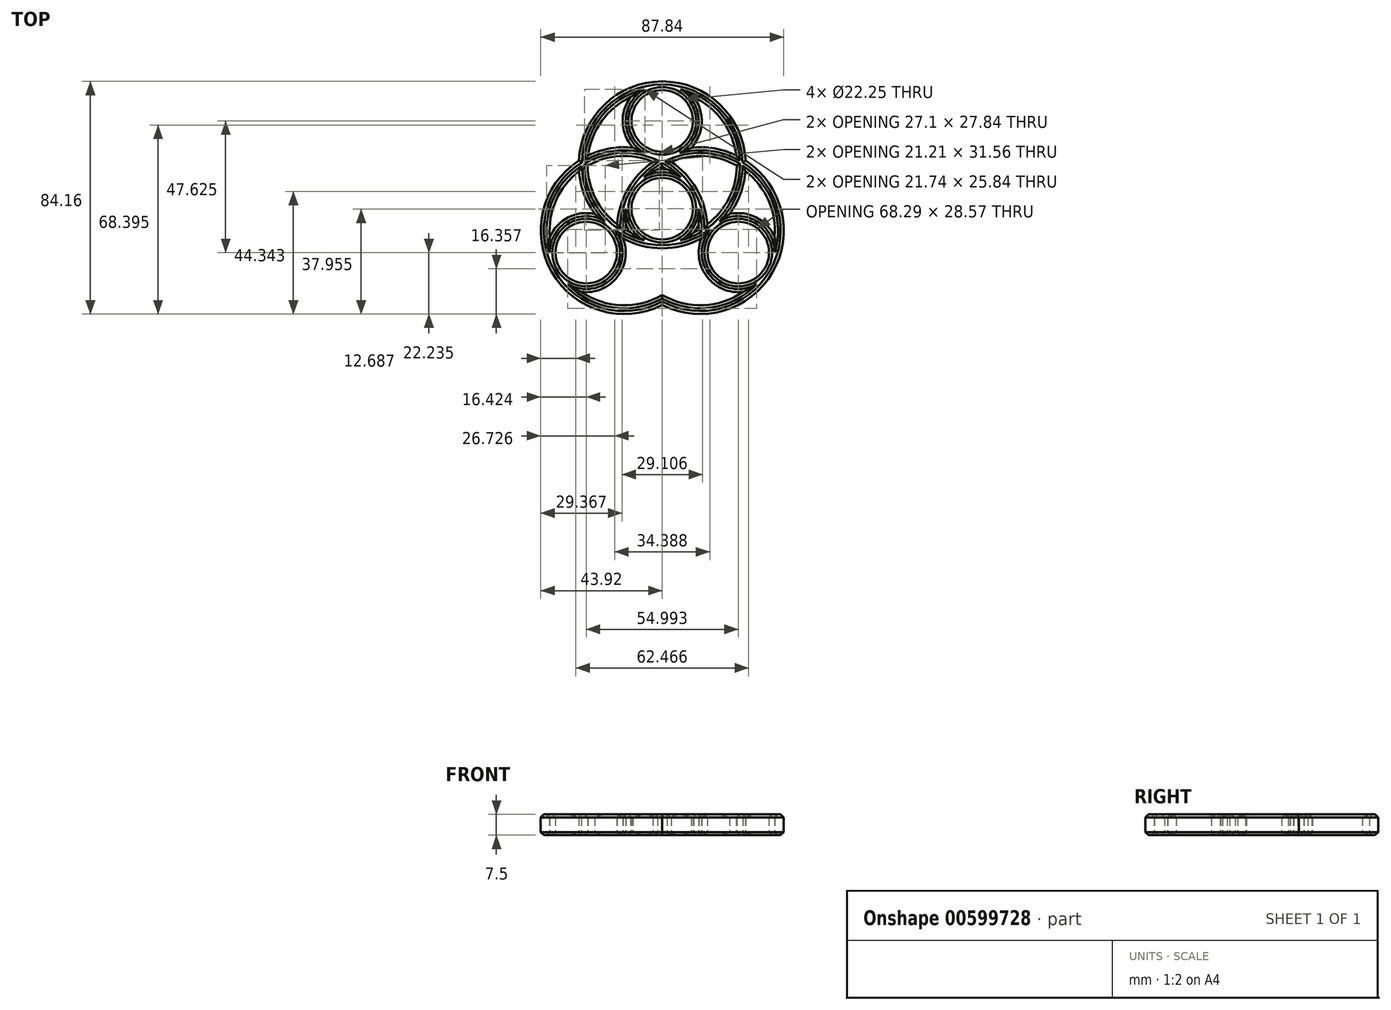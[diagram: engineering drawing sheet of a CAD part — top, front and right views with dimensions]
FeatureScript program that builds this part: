
annotation { "Feature Type Name" : "Feature", "Feature Type Description" : "" }
export const myFeature = defineFeature(function(context is Context, id is Id, definition is map)
    precondition{}
    {
        {
            var Q0;
            Q0=qCreatedBy(makeId("Top.planeOp"),FACE);
            var sketch = newSketch(context, id + "F0", { "sketchPlane" : qUnion([Q0])});
            skCircle(sketch, "E0", {"center": v(0, 0) * mm, "radius": 11.12 * mm});
            skCircle(sketch, "E1", {"center": v(0, 31.75) * mm, "radius": 11.12 * mm});
            skCircle(sketch, "E2", {"center": v(0, 31.75) * mm, "radius": 14.3 * mm});
            skCircle(sketch, "E3", {"center": v(0, 0) * mm, "radius": 14.3 * mm});
            skCircle(sketch, "E4", {"center": v(0, 15.88) * mm, "radius": 30.18 * mm});
            skCircle(sketch, "E5", {"center": v(0, 15.88) * mm, "radius": 27 * mm});
            skCircle(sketch, "E6.1.0", {"center": v(-27.5, -15.87) * mm, "radius": 11.12 * mm});
            skCircle(sketch, "E6.1.1", {"center": v(-27.5, -15.87) * mm, "radius": 14.3 * mm});
            skCircle(sketch, "E6.1.2", {"center": v(-13.75, -7.94) * mm, "radius": 27 * mm});
            skCircle(sketch, "E6.1.3", {"center": v(-13.75, -7.94) * mm, "radius": 30.18 * mm});
            skCircle(sketch, "E6.2.0", {"center": v(27.5, -15.88) * mm, "radius": 11.12 * mm});
            skCircle(sketch, "E6.2.1", {"center": v(27.5, -15.88) * mm, "radius": 14.3 * mm});
            skCircle(sketch, "E6.2.2", {"center": v(13.75, -7.94) * mm, "radius": 27 * mm});
            skCircle(sketch, "E6.2.3", {"center": v(13.75, -7.94) * mm, "radius": 30.18 * mm});
            skSolve(sketch);
        }
        {
            var Q0;
            Q0 = qSketchRegion(id + "F0", true);
            var Q1;
            {var subQ0=sQuery(id+"F0.wireOp",EDGE,"E6.1.3");var subQ1=sQuery(id+"F0.wireOp",EDGE,"E1");var subQ2=makeQuery(id+"F0.imprint","INTERSECT",VERTEX,{"disambiguationData":[OD(0.0)],"derivedFrom":[subQ1,subQ0]});Q1=makeQuery(id+"F0.imprint","IMPRINT",FACE,{"disambiguationData":[TD([[makeQuery(id+"F0.imprint","IMPRINT",EDGE,{"disambiguationData":[TD([[subQ2,1.0]])],"derivedFrom":subQ1}),-1.0]])]});}
            var Q2;
            {var subQ0=sQuery(id+"F0.wireOp",EDGE,"E5");var subQ1=sQuery(id+"F0.wireOp",EDGE,"E1");var subQ2=makeQuery(id+"F0.imprint","INTERSECT",VERTEX,{"derivedFrom":[subQ1,subQ0]});Q2=makeQuery(id+"F0.imprint","IMPRINT",FACE,{"disambiguationData":[TD([[makeQuery(id+"F0.imprint","IMPRINT",EDGE,{"disambiguationData":[TD([[subQ2,1.0]])],"derivedFrom":subQ1}),-1.0]])]});}
            var Q3;
            {var subQ0=sQuery(id+"F0.wireOp",EDGE,"E6.1.1");var subQ1=sQuery(id+"F0.wireOp",EDGE,"E4");var subQ2=makeQuery(id+"F0.imprint","INTERSECT",VERTEX,{"disambiguationData":[OD(0.0)],"derivedFrom":[subQ1,subQ0]});Q3=makeQuery(id+"F0.imprint","IMPRINT",FACE,{"disambiguationData":[TD([[makeQuery(id+"F0.imprint","IMPRINT",EDGE,{"disambiguationData":[TD([[subQ2,-1.0]])],"derivedFrom":subQ1}),-1.0]])]});}
            var Q4;
            {var subQ0=sQuery(id+"F0.wireOp",EDGE,"E6.2.3");var subQ1=sQuery(id+"F0.wireOp",EDGE,"E6.1.0");var subQ2=makeQuery(id+"F0.imprint","INTERSECT",VERTEX,{"disambiguationData":[OD(0.0)],"derivedFrom":[subQ1,subQ0]});Q4=makeQuery(id+"F0.imprint","IMPRINT",FACE,{"disambiguationData":[TD([[makeQuery(id+"F0.imprint","IMPRINT",EDGE,{"disambiguationData":[TD([[subQ2,1.0]])],"derivedFrom":subQ1}),-1.0]])]});}
            var Q5;
            {var subQ0=sQuery(id+"F0.wireOp",EDGE,"E6.2.1");var subQ1=sQuery(id+"F0.wireOp",EDGE,"E6.1.3");var subQ2=makeQuery(id+"F0.imprint","INTERSECT",VERTEX,{"disambiguationData":[OD(0.0)],"derivedFrom":[subQ1,subQ0]});Q5=makeQuery(id+"F0.imprint","IMPRINT",FACE,{"disambiguationData":[TD([[makeQuery(id+"F0.imprint","IMPRINT",EDGE,{"disambiguationData":[TD([[subQ2,-1.0]])],"derivedFrom":subQ1}),-1.0]])]});}
            var Q6;
            {var subQ0=sQuery(id+"F0.wireOp",EDGE,"E6.2.0");var subQ1=sQuery(id+"F0.wireOp",EDGE,"E4");var subQ2=makeQuery(id+"F0.imprint","INTERSECT",VERTEX,{"disambiguationData":[OD(1.0)],"derivedFrom":[subQ1,subQ0]});Q6=makeQuery(id+"F0.imprint","IMPRINT",FACE,{"disambiguationData":[TD([[makeQuery(id+"F0.imprint","IMPRINT",EDGE,{"disambiguationData":[TD([[subQ2,-1.0]])],"derivedFrom":subQ1}),-1.0]])]});}
            var Q7;
            {var subQ0=sQuery(id+"F0.wireOp",EDGE,"E6.2.2");var subQ1=sQuery(id+"F0.wireOp",EDGE,"E2");var subQ2=makeQuery(id+"F0.imprint","INTERSECT",VERTEX,{"disambiguationData":[OD(1.0)],"derivedFrom":[subQ1,subQ0]});Q7=makeQuery(id+"F0.imprint","IMPRINT",FACE,{"disambiguationData":[TD([[makeQuery(id+"F0.imprint","IMPRINT",EDGE,{"disambiguationData":[TD([[subQ2,-1.0]])],"derivedFrom":subQ1}),-1.0]])]});}
            var Q8;
            {var subQ3=sQuery(id+"F0.wireOp",EDGE,"E6.2.3");var subQ5=sQuery(id+"F0.wireOp",EDGE,"E1");var subQ6=makeQuery(id+"F0.imprint","INTERSECT",VERTEX,{"disambiguationData":[OD(0.0)],"derivedFrom":[subQ5,subQ3]});Q8=makeQuery(id+"F0.imprint","IMPRINT",FACE,{"disambiguationData":[TD([[makeQuery(id+"F0.imprint","IMPRINT",EDGE,{"disambiguationData":[TD([[subQ6,-1.0]])],"derivedFrom":subQ5}),-1.0]])]});}
            var Q9;
            {var subQ6=sQuery(id+"F0.wireOp",EDGE,"E6.1.3");var subQ8=sQuery(id+"F0.wireOp",EDGE,"E1");var subQ9=makeQuery(id+"F0.imprint","INTERSECT",VERTEX,{"disambiguationData":[OD(0.0)],"derivedFrom":[subQ8,subQ6]});Q9=makeQuery(id+"F0.imprint","IMPRINT",FACE,{"disambiguationData":[TD([[makeQuery(id+"F0.imprint","IMPRINT",EDGE,{"disambiguationData":[TD([[subQ9,-1.0]])],"derivedFrom":subQ8}),-1.0]])]});}
            var Q10;
            {var subQ0=sQuery(id+"F0.wireOp",EDGE,"E6.1.3");var subQ1=sQuery(id+"F0.wireOp",EDGE,"E2");var subQ2=makeQuery(id+"F0.imprint","INTERSECT",VERTEX,{"disambiguationData":[OD(0.0)],"derivedFrom":[subQ1,subQ0]});Q10=makeQuery(id+"F0.imprint","IMPRINT",FACE,{"disambiguationData":[TD([[makeQuery(id+"F0.imprint","IMPRINT",EDGE,{"disambiguationData":[TD([[subQ2,-1.0]])],"derivedFrom":subQ1}),-1.0]])]});}
            var Q11;
            {var subQ0=sQuery(id+"F0.wireOp",EDGE,"E6.1.3");var subQ1=sQuery(id+"F0.wireOp",EDGE,"E1");var subQ2=makeQuery(id+"F0.imprint","INTERSECT",VERTEX,{"disambiguationData":[OD(1.0)],"derivedFrom":[subQ1,subQ0]});Q11=makeQuery(id+"F0.imprint","IMPRINT",FACE,{"disambiguationData":[TD([[makeQuery(id+"F0.imprint","IMPRINT",EDGE,{"disambiguationData":[TD([[subQ2,-1.0]])],"derivedFrom":subQ1}),-1.0]])]});}
            var Q12;
            {var subQ0=sQuery(id+"F0.wireOp",EDGE,"E6.2.3");var subQ1=sQuery(id+"F0.wireOp",EDGE,"E2");var subQ2=makeQuery(id+"F0.imprint","INTERSECT",VERTEX,{"disambiguationData":[OD(0.0)],"derivedFrom":[subQ1,subQ0]});Q12=makeQuery(id+"F0.imprint","IMPRINT",FACE,{"disambiguationData":[TD([[makeQuery(id+"F0.imprint","IMPRINT",EDGE,{"disambiguationData":[TD([[subQ2,-1.0]])],"derivedFrom":subQ1}),1.0]])]});}
            var Q13;
            {var subQ1=sQuery(id+"F0.wireOp",EDGE,"E4");var subQ6=sQuery(id+"F0.wireOp",EDGE,"E6.1.1");var subQ7=makeQuery(id+"F0.imprint","INTERSECT",VERTEX,{"disambiguationData":[OD(0.0)],"derivedFrom":[subQ1,subQ6]});Q13=makeQuery(id+"F0.imprint","IMPRINT",FACE,{"disambiguationData":[TD([[makeQuery(id+"F0.imprint","IMPRINT",EDGE,{"disambiguationData":[TD([[subQ7,-1.0]])],"derivedFrom":subQ1}),1.0]])]});}
            var Q14;
            {var subQ1=sQuery(id+"F0.wireOp",EDGE,"E4");var subQ5=sQuery(id+"F0.wireOp",EDGE,"E6.2.3");var subQ11=makeQuery(id+"F0.imprint","INTERSECT",VERTEX,{"disambiguationData":[OD(1.0)],"derivedFrom":[subQ1,subQ5]});Q14=makeQuery(id+"F0.imprint","IMPRINT",FACE,{"disambiguationData":[TD([[makeQuery(id+"F0.imprint","IMPRINT",EDGE,{"disambiguationData":[TD([[subQ11,-1.0]])],"derivedFrom":subQ1}),-1.0]])]});}
            var Q15;
            {var subQ0=sQuery(id+"F0.wireOp",EDGE,"E6.1.0");var subQ1=sQuery(id+"F0.wireOp",EDGE,"E4");var subQ2=makeQuery(id+"F0.imprint","INTERSECT",VERTEX,{"disambiguationData":[OD(1.0)],"derivedFrom":[subQ1,subQ0]});Q15=makeQuery(id+"F0.imprint","IMPRINT",FACE,{"disambiguationData":[TD([[makeQuery(id+"F0.imprint","IMPRINT",EDGE,{"disambiguationData":[TD([[subQ2,-1.0]])],"derivedFrom":subQ1}),-1.0]])]});}
            var Q16;
            {var subQ0=sQuery(id+"F0.wireOp",EDGE,"E6.2.3");var subQ1=sQuery(id+"F0.wireOp",EDGE,"E4");var subQ2=makeQuery(id+"F0.imprint","INTERSECT",VERTEX,{"disambiguationData":[OD(1.0)],"derivedFrom":[subQ1,subQ0]});Q16=makeQuery(id+"F0.imprint","IMPRINT",FACE,{"disambiguationData":[TD([[makeQuery(id+"F0.imprint","IMPRINT",EDGE,{"disambiguationData":[TD([[subQ2,-1.0]])],"derivedFrom":subQ1}),1.0]])]});}
            var Q17;
            {var subQ0=sQuery(id+"F0.wireOp",EDGE,"E6.1.2");var subQ1=sQuery(id+"F0.wireOp",EDGE,"E4");var subQ2=makeQuery(id+"F0.imprint","INTERSECT",VERTEX,{"disambiguationData":[OD(0.0)],"derivedFrom":[subQ1,subQ0]});Q17=makeQuery(id+"F0.imprint","IMPRINT",FACE,{"disambiguationData":[TD([[makeQuery(id+"F0.imprint","IMPRINT",EDGE,{"disambiguationData":[TD([[subQ2,-1.0]])],"derivedFrom":subQ1}),1.0]])]});}
            var Q18;
            {var subQ0=sQuery(id+"F0.wireOp",EDGE,"E6.2.3");var subQ1=sQuery(id+"F0.wireOp",EDGE,"E6.1.1");var subQ2=makeQuery(id+"F0.imprint","INTERSECT",VERTEX,{"disambiguationData":[OD(0.0)],"derivedFrom":[subQ1,subQ0]});Q18=makeQuery(id+"F0.imprint","IMPRINT",FACE,{"disambiguationData":[TD([[makeQuery(id+"F0.imprint","IMPRINT",EDGE,{"disambiguationData":[TD([[subQ2,-1.0]])],"derivedFrom":subQ1}),-1.0]])]});}
            var Q19;
            {var subQ0=sQuery(id+"F0.wireOp",EDGE,"E6.2.2");var subQ1=sQuery(id+"F0.wireOp",EDGE,"E6.1.2");var subQ2=makeQuery(id+"F0.imprint","INTERSECT",VERTEX,{"disambiguationData":[OD(0.0)],"derivedFrom":[subQ1,subQ0]});Q19=makeQuery(id+"F0.imprint","IMPRINT",FACE,{"disambiguationData":[TD([[makeQuery(id+"F0.imprint","IMPRINT",EDGE,{"disambiguationData":[TD([[subQ2,-1.0]])],"derivedFrom":subQ1}),-1.0]])]});}
            var Q20;
            {var subQ1=sQuery(id+"F0.wireOp",EDGE,"E4");var subQ5=sQuery(id+"F0.wireOp",EDGE,"E6.2.1");var subQ11=makeQuery(id+"F0.imprint","INTERSECT",VERTEX,{"disambiguationData":[OD(0.0)],"derivedFrom":[subQ1,subQ5]});Q20=makeQuery(id+"F0.imprint","IMPRINT",FACE,{"disambiguationData":[TD([[makeQuery(id+"F0.imprint","IMPRINT",EDGE,{"disambiguationData":[TD([[subQ11,-1.0]])],"derivedFrom":subQ1}),-1.0]])]});}
            var Q21;
            {var subQ0=sQuery(id+"F0.wireOp",EDGE,"E6.2.1");var subQ1=sQuery(id+"F0.wireOp",EDGE,"E4");var subQ2=makeQuery(id+"F0.imprint","INTERSECT",VERTEX,{"disambiguationData":[OD(0.0)],"derivedFrom":[subQ1,subQ0]});Q21=makeQuery(id+"F0.imprint","IMPRINT",FACE,{"disambiguationData":[TD([[makeQuery(id+"F0.imprint","IMPRINT",EDGE,{"disambiguationData":[TD([[subQ2,-1.0]])],"derivedFrom":subQ1}),1.0]])]});}
            var Q22;
            {var subQ0=sQuery(id+"F0.wireOp",EDGE,"E6.1.3");var subQ1=sQuery(id+"F0.wireOp",EDGE,"E4");var subQ2=makeQuery(id+"F0.imprint","INTERSECT",VERTEX,{"disambiguationData":[OD(1.0)],"derivedFrom":[subQ1,subQ0]});Q22=makeQuery(id+"F0.imprint","IMPRINT",FACE,{"disambiguationData":[TD([[makeQuery(id+"F0.imprint","IMPRINT",EDGE,{"disambiguationData":[TD([[subQ2,-1.0]])],"derivedFrom":subQ1}),1.0]])]});}
            var Q23;
            {var subQ0=sQuery(id+"F0.wireOp",EDGE,"E6.1.3");var subQ1=sQuery(id+"F0.wireOp",EDGE,"E4");var subQ2=makeQuery(id+"F0.imprint","INTERSECT",VERTEX,{"disambiguationData":[OD(1.0)],"derivedFrom":[subQ1,subQ0]});Q23=makeQuery(id+"F0.imprint","IMPRINT",FACE,{"disambiguationData":[TD([[makeQuery(id+"F0.imprint","IMPRINT",EDGE,{"disambiguationData":[TD([[subQ2,-1.0]])],"derivedFrom":subQ1}),-1.0]])]});}
            var Q24;
            {var subQ0=sQuery(id+"F0.wireOp",EDGE,"E6.2.1");var subQ1=sQuery(id+"F0.wireOp",EDGE,"E4");var subQ2=makeQuery(id+"F0.imprint","INTERSECT",VERTEX,{"disambiguationData":[OD(1.0)],"derivedFrom":[subQ1,subQ0]});Q24=makeQuery(id+"F0.imprint","IMPRINT",FACE,{"disambiguationData":[TD([[makeQuery(id+"F0.imprint","IMPRINT",EDGE,{"disambiguationData":[TD([[subQ2,-1.0]])],"derivedFrom":subQ1}),1.0]])]});}
            var Q25;
            {var subQ0=sQuery(id+"F0.wireOp",EDGE,"E6.2.2");var subQ1=sQuery(id+"F0.wireOp",EDGE,"E3");var subQ2=makeQuery(id+"F0.imprint","INTERSECT",VERTEX,{"disambiguationData":[OD(0.0)],"derivedFrom":[subQ1,subQ0]});Q25=makeQuery(id+"F0.imprint","IMPRINT",FACE,{"disambiguationData":[TD([[makeQuery(id+"F0.imprint","IMPRINT",EDGE,{"disambiguationData":[TD([[subQ2,-1.0]])],"derivedFrom":subQ1}),1.0]])]});}
            var Q26;
            {var subQ0=sQuery(id+"F0.wireOp",EDGE,"E6.2.2");var subQ1=sQuery(id+"F0.wireOp",EDGE,"E0");var subQ2=makeQuery(id+"F0.imprint","INTERSECT",VERTEX,{"derivedFrom":[subQ1,subQ0]});Q26=makeQuery(id+"F0.imprint","IMPRINT",FACE,{"disambiguationData":[TD([[makeQuery(id+"F0.imprint","IMPRINT",EDGE,{"disambiguationData":[TD([[subQ2,-1.0]])],"derivedFrom":subQ1}),-1.0]])]});}
            var Q27;
            {var subQ0=sQuery(id+"F0.wireOp",EDGE,"E5");var subQ1=sQuery(id+"F0.wireOp",EDGE,"E3");var subQ2=makeQuery(id+"F0.imprint","INTERSECT",VERTEX,{"disambiguationData":[OD(0.0)],"derivedFrom":[subQ1,subQ0]});Q27=makeQuery(id+"F0.imprint","IMPRINT",FACE,{"disambiguationData":[TD([[makeQuery(id+"F0.imprint","IMPRINT",EDGE,{"disambiguationData":[TD([[subQ2,-1.0]])],"derivedFrom":subQ1}),1.0]])]});}
            var Q28;
            {var subQ0=sQuery(id+"F0.wireOp",EDGE,"E6.1.2");var subQ1=sQuery(id+"F0.wireOp",EDGE,"E0");var subQ2=makeQuery(id+"F0.imprint","INTERSECT",VERTEX,{"derivedFrom":[subQ1,subQ0]});Q28=makeQuery(id+"F0.imprint","IMPRINT",FACE,{"disambiguationData":[TD([[makeQuery(id+"F0.imprint","IMPRINT",EDGE,{"disambiguationData":[TD([[subQ2,1.0]])],"derivedFrom":subQ1}),-1.0]])]});}
            var Q29;
            {var subQ0=sQuery(id+"F0.wireOp",EDGE,"E6.1.2");var subQ1=sQuery(id+"F0.wireOp",EDGE,"E3");var subQ2=makeQuery(id+"F0.imprint","INTERSECT",VERTEX,{"disambiguationData":[OD(0.0)],"derivedFrom":[subQ1,subQ0]});Q29=makeQuery(id+"F0.imprint","IMPRINT",FACE,{"disambiguationData":[TD([[makeQuery(id+"F0.imprint","IMPRINT",EDGE,{"disambiguationData":[TD([[subQ2,1.0]])],"derivedFrom":subQ1}),1.0]])]});}
            var Q30;
            {var subQ0=sQuery(id+"F0.wireOp",EDGE,"E6.1.2");var subQ1=sQuery(id+"F0.wireOp",EDGE,"E3");var subQ2=makeQuery(id+"F0.imprint","INTERSECT",VERTEX,{"disambiguationData":[OD(0.0)],"derivedFrom":[subQ1,subQ0]});Q30=makeQuery(id+"F0.imprint","IMPRINT",FACE,{"disambiguationData":[TD([[makeQuery(id+"F0.imprint","IMPRINT",EDGE,{"disambiguationData":[TD([[subQ2,1.0]])],"derivedFrom":subQ1}),-1.0]])]});}
            var Q31;
            {var subQ5=sQuery(id+"F0.wireOp",EDGE,"E6.2.3");var subQ7=sQuery(id+"F0.wireOp",EDGE,"E2");var subQ9=makeQuery(id+"F0.imprint","INTERSECT",VERTEX,{"disambiguationData":[OD(0.0)],"derivedFrom":[subQ7,subQ5]});Q31=makeQuery(id+"F0.imprint","IMPRINT",FACE,{"disambiguationData":[TD([[makeQuery(id+"F0.imprint","IMPRINT",EDGE,{"disambiguationData":[TD([[subQ9,-1.0]])],"derivedFrom":subQ7}),-1.0]])]});}
            var Q32;
            {var subQ0=sQuery(id+"F0.wireOp",EDGE,"E6.2.2");var subQ1=sQuery(id+"F0.wireOp",EDGE,"E3");var subQ2=makeQuery(id+"F0.imprint","INTERSECT",VERTEX,{"disambiguationData":[OD(0.0)],"derivedFrom":[subQ1,subQ0]});Q32=makeQuery(id+"F0.imprint","IMPRINT",FACE,{"disambiguationData":[TD([[makeQuery(id+"F0.imprint","IMPRINT",EDGE,{"disambiguationData":[TD([[subQ2,-1.0]])],"derivedFrom":subQ1}),-1.0]])]});}
            var Q33;
            {var subQ0=sQuery(id+"F0.wireOp",EDGE,"E6.2.3");var subQ1=sQuery(id+"F0.wireOp",EDGE,"E3");var subQ2=makeQuery(id+"F0.imprint","INTERSECT",VERTEX,{"derivedFrom":[subQ1,subQ0]});Q33=makeQuery(id+"F0.imprint","IMPRINT",FACE,{"disambiguationData":[TD([[makeQuery(id+"F0.imprint","IMPRINT",EDGE,{"disambiguationData":[TD([[subQ2,-1.0]])],"derivedFrom":subQ1}),-1.0]])]});}
            var Q34;
            {var subQ1=sQuery(id+"F0.wireOp",EDGE,"E4");var subQ5=sQuery(id+"F0.wireOp",EDGE,"E6.1.1");var subQ6=makeQuery(id+"F0.imprint","INTERSECT",VERTEX,{"disambiguationData":[OD(1.0)],"derivedFrom":[subQ1,subQ5]});Q34=makeQuery(id+"F0.imprint","IMPRINT",FACE,{"disambiguationData":[TD([[makeQuery(id+"F0.imprint","IMPRINT",EDGE,{"disambiguationData":[TD([[subQ6,-1.0]])],"derivedFrom":subQ1}),1.0]])]});}
            var Q35;
            {var subQ0=sQuery(id+"F0.wireOp",EDGE,"E5");var subQ1=sQuery(id+"F0.wireOp",EDGE,"E3");var subQ2=makeQuery(id+"F0.imprint","INTERSECT",VERTEX,{"disambiguationData":[OD(0.0)],"derivedFrom":[subQ1,subQ0]});Q35=makeQuery(id+"F0.imprint","IMPRINT",FACE,{"disambiguationData":[TD([[makeQuery(id+"F0.imprint","IMPRINT",EDGE,{"disambiguationData":[TD([[subQ2,-1.0]])],"derivedFrom":subQ1}),-1.0]])]});}
            var Q36;
            {var subQ0=sQuery(id+"F0.wireOp",EDGE,"E4");var subQ1=sQuery(id+"F0.wireOp",EDGE,"E3");var subQ2=makeQuery(id+"F0.imprint","INTERSECT",VERTEX,{"derivedFrom":[subQ1,subQ0]});Q36=makeQuery(id+"F0.imprint","IMPRINT",FACE,{"disambiguationData":[TD([[makeQuery(id+"F0.imprint","IMPRINT",EDGE,{"disambiguationData":[TD([[subQ2,-1.0]])],"derivedFrom":subQ1}),-1.0]])]});}
            var Q37;
            {var subQ5=sQuery(id+"F0.wireOp",EDGE,"E6.1.2");var subQ6=sQuery(id+"F0.wireOp",EDGE,"E4");var subQ7=makeQuery(id+"F0.imprint","INTERSECT",VERTEX,{"disambiguationData":[OD(1.0)],"derivedFrom":[subQ6,subQ5]});Q37=makeQuery(id+"F0.imprint","IMPRINT",FACE,{"disambiguationData":[TD([[makeQuery(id+"F0.imprint","IMPRINT",EDGE,{"disambiguationData":[TD([[subQ7,-1.0]])],"derivedFrom":subQ6}),1.0]])]});}
            var Q38;
            {var subQ0=sQuery(id+"F0.wireOp",EDGE,"E6.1.3");var subQ1=sQuery(id+"F0.wireOp",EDGE,"E3");var subQ2=makeQuery(id+"F0.imprint","INTERSECT",VERTEX,{"derivedFrom":[subQ1,subQ0]});Q38=makeQuery(id+"F0.imprint","IMPRINT",FACE,{"disambiguationData":[TD([[makeQuery(id+"F0.imprint","IMPRINT",EDGE,{"disambiguationData":[TD([[subQ2,1.0]])],"derivedFrom":subQ1}),-1.0]])]});}
            var Q39;
            {var subQ3=sQuery(id+"F0.wireOp",EDGE,"E6.1.3");var subQ5=sQuery(id+"F0.wireOp",EDGE,"E2");var subQ6=makeQuery(id+"F0.imprint","INTERSECT",VERTEX,{"disambiguationData":[OD(1.0)],"derivedFrom":[subQ5,subQ3]});Q39=makeQuery(id+"F0.imprint","IMPRINT",FACE,{"disambiguationData":[TD([[makeQuery(id+"F0.imprint","IMPRINT",EDGE,{"disambiguationData":[TD([[subQ6,-1.0]])],"derivedFrom":subQ5}),-1.0]])]});}
            var Q40;
            {var subQ0=sQuery(id+"F0.wireOp",EDGE,"E6.2.2");var subQ1=sQuery(id+"F0.wireOp",EDGE,"E0");var subQ2=makeQuery(id+"F0.imprint","INTERSECT",VERTEX,{"derivedFrom":[subQ1,subQ0]});Q40=makeQuery(id+"F0.imprint","IMPRINT",FACE,{"disambiguationData":[TD([[makeQuery(id+"F0.imprint","IMPRINT",EDGE,{"disambiguationData":[TD([[subQ2,1.0]])],"derivedFrom":subQ1}),-1.0]])]});}
            var Q41;
            {var subQ0=sQuery(id+"F0.wireOp",EDGE,"E6.1.3");var subQ1=sQuery(id+"F0.wireOp",EDGE,"E2");var subQ2=makeQuery(id+"F0.imprint","INTERSECT",VERTEX,{"disambiguationData":[OD(1.0)],"derivedFrom":[subQ1,subQ0]});Q41=makeQuery(id+"F0.imprint","IMPRINT",FACE,{"disambiguationData":[TD([[makeQuery(id+"F0.imprint","IMPRINT",EDGE,{"disambiguationData":[TD([[subQ2,-1.0]])],"derivedFrom":subQ1}),1.0]])]});}
            var Q42;
            {var subQ0=sQuery(id+"F0.wireOp",EDGE,"E6.1.3");var subQ1=sQuery(id+"F0.wireOp",EDGE,"E2");var subQ2=makeQuery(id+"F0.imprint","INTERSECT",VERTEX,{"disambiguationData":[OD(0.0)],"derivedFrom":[subQ1,subQ0]});Q42=makeQuery(id+"F0.imprint","IMPRINT",FACE,{"disambiguationData":[TD([[makeQuery(id+"F0.imprint","IMPRINT",EDGE,{"disambiguationData":[TD([[subQ2,-1.0]])],"derivedFrom":subQ1}),1.0]])]});}
            extrude(context, id + "F1", {"entities" : qUnion([Q0, Q1, Q2, Q3, Q4, Q5, Q6, Q7, Q8, Q9, Q10, Q11, Q12, Q13, Q14, Q15, Q16, Q17, Q18, Q19, Q20, Q21, Q22, Q23, Q24, Q25, Q26, Q27, Q28, Q29, Q30, Q31, Q32, Q33, Q34, Q35, Q36, Q37, Q38, Q39, Q40, Q41, Q42]), "depth" : 7.5 * mm, "offsetDistance" : 25.4 * mm});
        }
        {
            var Q0;
            Q0=makeQuery(id+"F1.opExtrude","CAP_FACE",FACE,{"disambiguationData":[OSD([sQuery(id+"F0.wireOp",EDGE,"E0"),sQuery(id+"F0.wireOp",EDGE,"E1"),sQuery(id+"F0.wireOp",EDGE,"E2"),sQuery(id+"F0.wireOp",EDGE,"E3"),sQuery(id+"F0.wireOp",EDGE,"E4"),sQuery(id+"F0.wireOp",EDGE,"E5"),sQuery(id+"F0.wireOp",EDGE,"E6.1.0"),sQuery(id+"F0.wireOp",EDGE,"E6.1.1"),sQuery(id+"F0.wireOp",EDGE,"E6.1.2"),sQuery(id+"F0.wireOp",EDGE,"E6.1.3"),sQuery(id+"F0.wireOp",EDGE,"E6.2.0"),sQuery(id+"F0.wireOp",EDGE,"E6.2.1"),sQuery(id+"F0.wireOp",EDGE,"E6.2.2"),sQuery(id+"F0.wireOp",EDGE,"E6.2.3")])],"isStart":false});
            var Q1;
            Q1=makeQuery(id+"F1.opExtrude","CAP_FACE",FACE,{"disambiguationData":[OSD([sQuery(id+"F0.wireOp",EDGE,"E0"),sQuery(id+"F0.wireOp",EDGE,"E1"),sQuery(id+"F0.wireOp",EDGE,"E2"),sQuery(id+"F0.wireOp",EDGE,"E3"),sQuery(id+"F0.wireOp",EDGE,"E4"),sQuery(id+"F0.wireOp",EDGE,"E5"),sQuery(id+"F0.wireOp",EDGE,"E6.1.0"),sQuery(id+"F0.wireOp",EDGE,"E6.1.1"),sQuery(id+"F0.wireOp",EDGE,"E6.1.2"),sQuery(id+"F0.wireOp",EDGE,"E6.1.3"),sQuery(id+"F0.wireOp",EDGE,"E6.2.0"),sQuery(id+"F0.wireOp",EDGE,"E6.2.1"),sQuery(id+"F0.wireOp",EDGE,"E6.2.2"),sQuery(id+"F0.wireOp",EDGE,"E6.2.3")])],"isStart":true});
            chamfer(context, id + "F2", {"entities" : qUnion([Q0, Q1]), "width" : 1.1 * mm, "tangentPropagation" : true});
        }
    });
